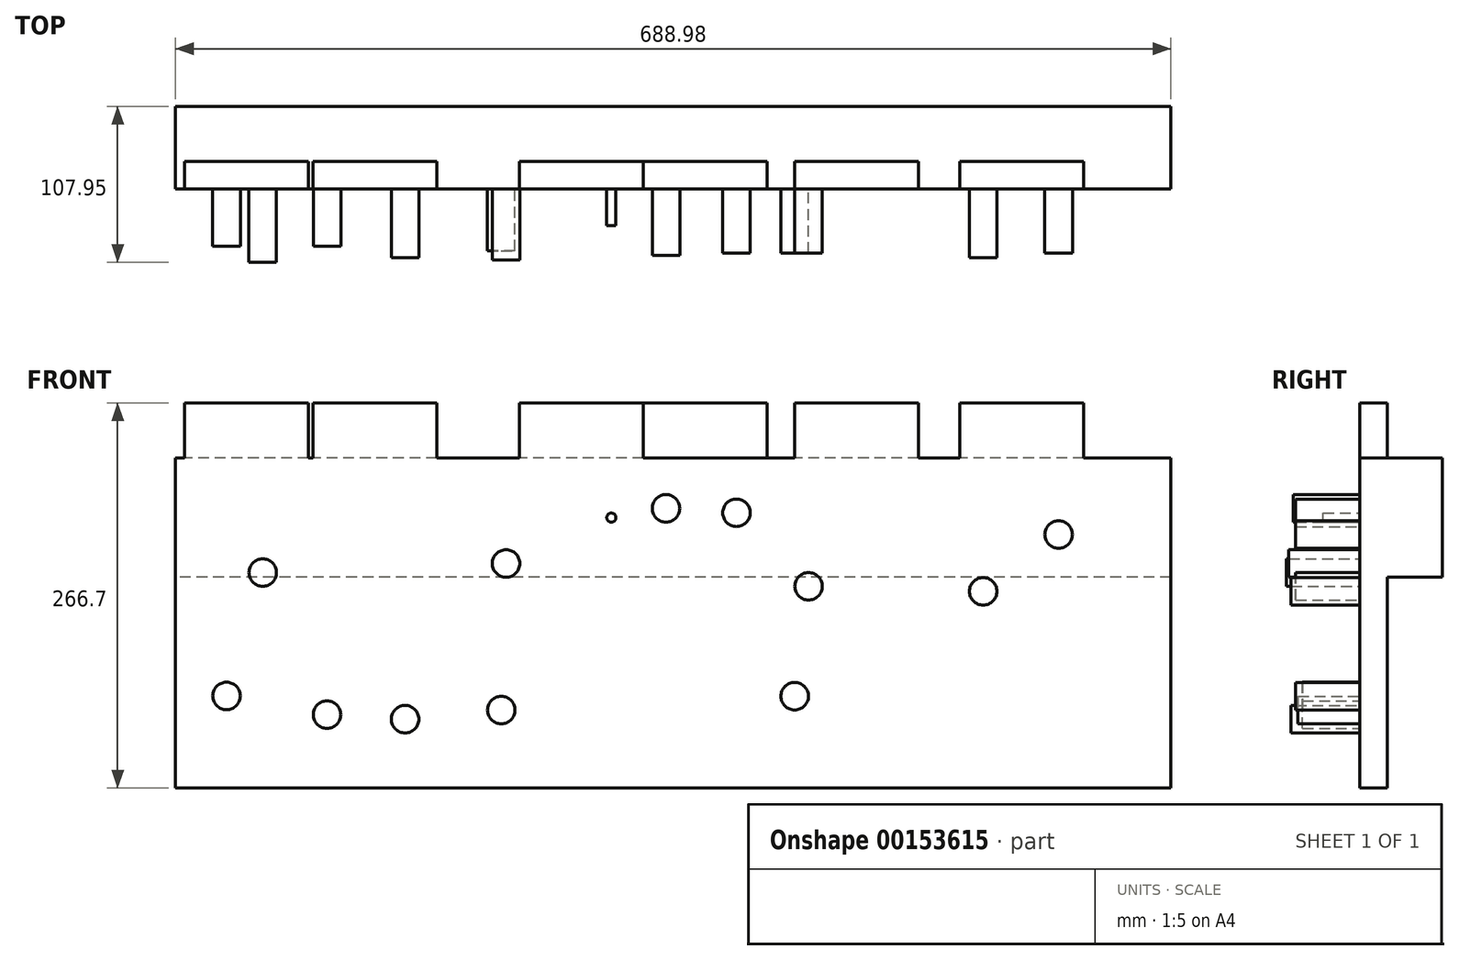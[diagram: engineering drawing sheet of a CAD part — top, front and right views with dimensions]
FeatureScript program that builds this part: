
annotation { "Feature Type Name" : "Feature", "Feature Type Description" : "" }
export const myFeature = defineFeature(function(context is Context, id is Id, definition is map)
    precondition{}
    {
        {
            var Q0;
            Q0=qCreatedBy(makeId("Front.planeOp"),FACE);
            var sketch = newSketch(context, id + "F0", { "sketchPlane" : qUnion([Q0])});
            skLineSegment(sketch, "E0.bottom", {"start": v(344.49, -114.3) * mm, "end": v(-344.49, -114.3) * mm});
            skLineSegment(sketch, "E0.top", {"start": v(344.49, 114.3) * mm, "end": v(-344.49, 114.3) * mm});
            skLineSegment(sketch, "E0.left", {"start": v(344.49, -114.3) * mm, "end": v(344.49, 114.3) * mm});
            skLineSegment(sketch, "E0.right", {"start": v(-344.49, -114.3) * mm, "end": v(-344.49, 114.3) * mm});
            skPoint(sketch, "E0.middle", {"position": v(0, 0) * mm});
            skSolve(sketch);
        }
        {
            var Q0;
            Q0 = qSketchRegion(id + "F0", true);
            extrude(context, id + "F1", {"entities" : qUnion([Q0]), "depth" : 19.05 * mm});
        }
        {
            var Q0;
            Q0=makeQuery(id+"F1.opExtrude","CAP_FACE",FACE,{"disambiguationData":[OSD([sQuery(id+"F0.wireOp",EDGE,"E0.bottom"),sQuery(id+"F0.wireOp",EDGE,"E0.top"),sQuery(id+"F0.wireOp",EDGE,"E0.left"),sQuery(id+"F0.wireOp",EDGE,"E0.right")])],"isStart":true});
            var sketch = newSketch(context, id + "F2", { "sketchPlane" : qUnion([Q0])});
            skLineSegment(sketch, "E1.bottom", {"start": v(-344.49, 114.3) * mm, "end": v(344.49, 114.3) * mm});
            skLineSegment(sketch, "E1.top", {"start": v(-344.49, 31.75) * mm, "end": v(344.49, 31.75) * mm});
            skLineSegment(sketch, "E1.left", {"start": v(-344.49, 114.3) * mm, "end": v(-344.49, 31.75) * mm});
            skLineSegment(sketch, "E1.right", {"start": v(344.49, 114.3) * mm, "end": v(344.49, 31.75) * mm});
            skSolve(sketch);
        }
        {
            var Q0;
            Q0 = qSketchRegion(id + "F2", true);
            extrude(context, id + "F3", {"entities" : qUnion([Q0]), "depth" : 38.1 * mm});
        }
        {
            var Q0;
            Q0=makeQuery(id+"F1.opExtrude","CAP_FACE",FACE,{"disambiguationData":[OSD([sQuery(id+"F0.wireOp",EDGE,"E0.bottom"),sQuery(id+"F0.wireOp",EDGE,"E0.top"),sQuery(id+"F0.wireOp",EDGE,"E0.left"),sQuery(id+"F0.wireOp",EDGE,"E0.right")])],"isStart":false});
            var sketch = newSketch(context, id + "F4", { "sketchPlane" : qUnion([Q0])});
            skCircle(sketch, "E2", {"center": v(-284.18, 34.92) * mm, "radius": 9.53 * mm});
            skCircle(sketch, "E3", {"center": v(-115.78, 41.23) * mm, "radius": 9.53 * mm});
            skCircle(sketch, "E4", {"center": v(-5.07, 79.42) * mm, "radius": 9.52 * mm});
            skCircle(sketch, "E5", {"center": v(43.71, 76.35) * mm, "radius": 9.53 * mm});
            skCircle(sketch, "E6", {"center": v(266.7, 61.27) * mm, "radius": 9.53 * mm});
            skCircle(sketch, "E7", {"center": v(-309.24, -50.51) * mm, "radius": 9.53 * mm});
            skCircle(sketch, "E8", {"center": v(-239.7, -63.5) * mm, "radius": 9.53 * mm});
            skCircle(sketch, "E9", {"center": v(-185.67, -66.62) * mm, "radius": 9.53 * mm});
            skCircle(sketch, "E10", {"center": v(-119.06, -60.3) * mm, "radius": 9.53 * mm});
            skCircle(sketch, "E11", {"center": v(93.64, 25.43) * mm, "radius": 9.53 * mm});
            skCircle(sketch, "E12", {"center": v(214.5, 21.94) * mm, "radius": 9.53 * mm});
            skCircle(sketch, "E13", {"center": v(84.02, -50.69) * mm, "radius": 9.53 * mm});
            skCircle(sketch, "E14", {"center": v(-42.88, 73) * mm, "radius": 3.18 * mm});
            skSolve(sketch);
        }
        {
            var Q0;
            Q0=makeQuery(id+"F4.imprint","IMPRINT",FACE,{"disambiguationData":[TD([[makeQuery(id+"F4.imprint","IMPRINT",EDGE,{"derivedFrom":sQuery(id+"F4.wireOp",EDGE,"E2")}),1.0]])]});
            var Q1;
            Q1=sQuery(id+"F4.wireOp",EDGE,"E2");
            extrude(context, id + "F5", {"entities" : qUnion([Q0]), "operationType" : NewBodyOperationType.ADD, "surfaceEntities" : qUnion([Q1]), "depth" : 50.8 * mm});
        }
        {
            var Q0;
            Q0=makeQuery(id+"F4.imprint","IMPRINT",FACE,{"disambiguationData":[TD([[makeQuery(id+"F4.imprint","IMPRINT",EDGE,{"derivedFrom":sQuery(id+"F4.wireOp",EDGE,"E3")}),1.0]])]});
            var Q1;
            Q1=sQuery(id+"F4.wireOp",EDGE,"E3");
            extrude(context, id + "F6", {"entities" : qUnion([Q0]), "operationType" : NewBodyOperationType.ADD, "surfaceEntities" : qUnion([Q1]), "depth" : 49.2 * mm});
        }
        {
            var Q0;
            Q0=makeQuery(id+"F4.imprint","IMPRINT",FACE,{"disambiguationData":[TD([[makeQuery(id+"F4.imprint","IMPRINT",EDGE,{"derivedFrom":sQuery(id+"F4.wireOp",EDGE,"E4")}),1.0]])]});
            var Q1;
            Q1=sQuery(id+"F4.wireOp",EDGE,"E4");
            extrude(context, id + "F7", {"entities" : qUnion([Q0]), "operationType" : NewBodyOperationType.ADD, "surfaceEntities" : qUnion([Q1]), "depth" : 46.04 * mm});
        }
        {
            var Q0;
            Q0=makeQuery(id+"F4.imprint","IMPRINT",FACE,{"disambiguationData":[TD([[makeQuery(id+"F4.imprint","IMPRINT",EDGE,{"derivedFrom":sQuery(id+"F4.wireOp",EDGE,"E5")}),1.0]])]});
            var Q1;
            Q1=sQuery(id+"F4.wireOp",EDGE,"E5");
            extrude(context, id + "F8", {"entities" : qUnion([Q0]), "operationType" : NewBodyOperationType.ADD, "surfaceEntities" : qUnion([Q1]), "depth" : 44.45 * mm});
        }
        {
            var Q0;
            Q0=makeQuery(id+"F4.imprint","IMPRINT",FACE,{"disambiguationData":[TD([[makeQuery(id+"F4.imprint","IMPRINT",EDGE,{"derivedFrom":sQuery(id+"F4.wireOp",EDGE,"E6")}),1.0]])]});
            var Q1;
            Q1=sQuery(id+"F4.wireOp",EDGE,"E6");
            extrude(context, id + "F9", {"entities" : qUnion([Q0]), "operationType" : NewBodyOperationType.ADD, "surfaceEntities" : qUnion([Q1]), "depth" : 44.45 * mm});
        }
        {
            var Q0;
            Q0=makeQuery(id+"F4.imprint","IMPRINT",FACE,{"disambiguationData":[TD([[makeQuery(id+"F4.imprint","IMPRINT",EDGE,{"derivedFrom":sQuery(id+"F4.wireOp",EDGE,"E7")}),1.0]])]});
            var Q1;
            Q1=sQuery(id+"F4.wireOp",EDGE,"E7");
            extrude(context, id + "F10", {"entities" : qUnion([Q0]), "operationType" : NewBodyOperationType.ADD, "surfaceEntities" : qUnion([Q1]), "depth" : 39.69 * mm});
        }
        {
            var Q0;
            Q0=makeQuery(id+"F4.imprint","IMPRINT",FACE,{"disambiguationData":[TD([[makeQuery(id+"F4.imprint","IMPRINT",EDGE,{"derivedFrom":sQuery(id+"F4.wireOp",EDGE,"E8")}),1.0]])]});
            extrude(context, id + "F11", {"entities" : qUnion([Q0]), "operationType" : NewBodyOperationType.ADD, "depth" : 39.69 * mm});
        }
        {
            var Q0;
            Q0=makeQuery(id+"F4.imprint","IMPRINT",FACE,{"disambiguationData":[TD([[makeQuery(id+"F4.imprint","IMPRINT",EDGE,{"derivedFrom":sQuery(id+"F4.wireOp",EDGE,"E9")}),1.0]])]});
            var Q1;
            Q1=sQuery(id+"F4.wireOp",EDGE,"E9");
            extrude(context, id + "F12", {"entities" : qUnion([Q0]), "operationType" : NewBodyOperationType.ADD, "surfaceEntities" : qUnion([Q1]), "depth" : 47.62 * mm});
        }
        {
            var Q0;
            Q0=makeQuery(id+"F4.imprint","IMPRINT",FACE,{"disambiguationData":[TD([[makeQuery(id+"F4.imprint","IMPRINT",EDGE,{"derivedFrom":sQuery(id+"F4.wireOp",EDGE,"E10")}),1.0]])]});
            extrude(context, id + "F13", {"entities" : qUnion([Q0]), "operationType" : NewBodyOperationType.ADD, "depth" : 42.86 * mm});
        }
        {
            var Q0;
            Q0=makeQuery(id+"F4.imprint","IMPRINT",FACE,{"disambiguationData":[TD([[makeQuery(id+"F4.imprint","IMPRINT",EDGE,{"derivedFrom":sQuery(id+"F4.wireOp",EDGE,"E11")}),1.0]])]});
            extrude(context, id + "F14", {"entities" : qUnion([Q0]), "operationType" : NewBodyOperationType.ADD, "depth" : 44.45 * mm});
        }
        {
            var Q0;
            Q0=makeQuery(id+"F4.imprint","IMPRINT",FACE,{"disambiguationData":[TD([[makeQuery(id+"F4.imprint","IMPRINT",EDGE,{"derivedFrom":sQuery(id+"F4.wireOp",EDGE,"E12")}),1.0]])]});
            extrude(context, id + "F15", {"entities" : qUnion([Q0]), "operationType" : NewBodyOperationType.ADD, "depth" : 47.62 * mm});
        }
        {
            var Q0;
            Q0=makeQuery(id+"F4.imprint","IMPRINT",FACE,{"disambiguationData":[TD([[makeQuery(id+"F4.imprint","IMPRINT",EDGE,{"derivedFrom":sQuery(id+"F4.wireOp",EDGE,"E13")}),1.0]])]});
            extrude(context, id + "F16", {"entities" : qUnion([Q0]), "operationType" : NewBodyOperationType.ADD, "depth" : 44.45 * mm});
        }
        {
            var Q0;
            Q0=makeQuery(id+"F4.imprint","IMPRINT",FACE,{"disambiguationData":[TD([[makeQuery(id+"F4.imprint","IMPRINT",EDGE,{"derivedFrom":sQuery(id+"F4.wireOp",EDGE,"E14")}),1.0]])]});
            extrude(context, id + "F17", {"entities" : qUnion([Q0]), "operationType" : NewBodyOperationType.ADD, "depth" : 25.4 * mm});
        }
        {
            var Q0;
            Q0=makeQuery(id+"F1.opExtrude","SWEPT_FACE",FACE,{"disambiguationData":[OSD([sQuery(id+"F0.wireOp",EDGE,"E0.top")])]});
            var sketch = newSketch(context, id + "F18", { "sketchPlane" : qUnion([Q0])});
            skLineSegment(sketch, "E15.left", {"start": v(-338.14, -19.05) * mm, "end": v(-338.14, -19.05) * mm});
            skLineSegment(sketch, "E15.right", {"start": v(-299.87, -19.05) * mm, "end": v(-299.87, -19.05) * mm});
            skLineSegment(sketch, "E16.bottom", {"start": v(-338.14, -19.05) * mm, "end": v(-252.41, -19.05) * mm});
            skLineSegment(sketch, "E16.top", {"start": v(-338.14, 0) * mm, "end": v(-252.41, 0) * mm});
            skLineSegment(sketch, "E16.left", {"start": v(-338.14, -19.05) * mm, "end": v(-338.14, 0) * mm});
            skLineSegment(sketch, "E16.right", {"start": v(-252.41, -19.05) * mm, "end": v(-252.41, 0) * mm});
            skLineSegment(sketch, "E17", {"start": v(-252.41, -19.05) * mm, "end": v(-249.24, -19.05) * mm, "construction": true});
            skLineSegment(sketch, "E18.bottom", {"start": v(-249.24, -19.05) * mm, "end": v(-163.51, -19.05) * mm});
            skLineSegment(sketch, "E18.top", {"start": v(-249.24, 0) * mm, "end": v(-163.51, 0) * mm});
            skLineSegment(sketch, "E18.left", {"start": v(-249.24, -19.05) * mm, "end": v(-249.24, 0) * mm});
            skLineSegment(sketch, "E18.right", {"start": v(-163.51, -19.05) * mm, "end": v(-163.51, 0) * mm});
            skLineSegment(sketch, "E19", {"start": v(-163.51, -19.05) * mm, "end": v(-106.36, -19.05) * mm, "construction": true});
            skLineSegment(sketch, "E20.bottom", {"start": v(-106.36, -19.05) * mm, "end": v(-20.64, -19.05) * mm});
            skLineSegment(sketch, "E20.top", {"start": v(-106.36, 0) * mm, "end": v(-20.64, 0) * mm});
            skLineSegment(sketch, "E20.left", {"start": v(-106.36, -19.05) * mm, "end": v(-106.36, 0) * mm});
            skLineSegment(sketch, "E20.right", {"start": v(-20.64, -19.05) * mm, "end": v(-20.64, 0) * mm});
            skLineSegment(sketch, "E21.bottom", {"start": v(-20.64, -19.05) * mm, "end": v(65.09, -19.05) * mm});
            skLineSegment(sketch, "E21.top", {"start": v(-20.64, 0) * mm, "end": v(65.09, 0) * mm});
            skLineSegment(sketch, "E21.right", {"start": v(65.09, -19.05) * mm, "end": v(65.09, 0) * mm});
            skLineSegment(sketch, "E22", {"start": v(65.09, -19.05) * mm, "end": v(84.14, -19.05) * mm});
            skLineSegment(sketch, "E23.bottom", {"start": v(84.14, -19.05) * mm, "end": v(169.86, -19.05) * mm});
            skLineSegment(sketch, "E23.top", {"start": v(84.14, 0) * mm, "end": v(169.86, 0) * mm});
            skLineSegment(sketch, "E23.left", {"start": v(84.14, -19.05) * mm, "end": v(84.14, 0) * mm});
            skLineSegment(sketch, "E23.right", {"start": v(169.86, -19.05) * mm, "end": v(169.86, 0) * mm});
            skLineSegment(sketch, "E24", {"start": v(169.86, -19.05) * mm, "end": v(198.44, -19.05) * mm, "construction": true});
            skLineSegment(sketch, "E25.bottom", {"start": v(198.44, -19.05) * mm, "end": v(284.16, -19.05) * mm});
            skLineSegment(sketch, "E25.top", {"start": v(198.44, 0) * mm, "end": v(284.16, 0) * mm});
            skLineSegment(sketch, "E25.left", {"start": v(198.44, -19.05) * mm, "end": v(198.44, 0) * mm});
            skLineSegment(sketch, "E25.right", {"start": v(284.16, -19.05) * mm, "end": v(284.16, 0) * mm});
            skSolve(sketch);
        }
        {
            var Q0;
            Q0=makeQuery(id+"F18.imprint","IMPRINT",FACE,{"disambiguationData":[TD([[makeQuery(id+"F18.imprint","IMPRINT",EDGE,{"derivedFrom":sQuery(id+"F18.wireOp",EDGE,"E16.bottom")}),-1.0]])]});
            extrude(context, id + "F19", {"entities" : qUnion([Q0]), "operationType" : NewBodyOperationType.ADD, "depth" : 38.1 * mm});
        }
        {
            var Q0;
            Q0=makeQuery(id+"F18.imprint","IMPRINT",FACE,{"disambiguationData":[TD([[makeQuery(id+"F18.imprint","IMPRINT",EDGE,{"derivedFrom":sQuery(id+"F18.wireOp",EDGE,"E18.bottom")}),-1.0]])]});
            var Q1;
            Q1=makeQuery(id+"F18.imprint","IMPRINT",FACE,{"disambiguationData":[TD([[makeQuery(id+"F18.imprint","IMPRINT",EDGE,{"derivedFrom":sQuery(id+"F18.wireOp",EDGE,"E20.bottom")}),-1.0]])]});
            extrude(context, id + "F20", {"entities" : qUnion([Q0, Q1]), "operationType" : NewBodyOperationType.ADD, "depth" : 38.1 * mm});
        }
        {
            var Q0;
            Q0=makeQuery(id+"F18.imprint","IMPRINT",FACE,{"disambiguationData":[TD([[makeQuery(id+"F18.imprint","IMPRINT",EDGE,{"derivedFrom":sQuery(id+"F18.wireOp",EDGE,"E21.bottom")}),-1.0]])]});
            extrude(context, id + "F21", {"entities" : qUnion([Q0]), "depth" : 38.1 * mm});
        }
        {
            var Q0;
            Q0=makeQuery(id+"F18.imprint","IMPRINT",FACE,{"disambiguationData":[TD([[makeQuery(id+"F18.imprint","IMPRINT",EDGE,{"derivedFrom":sQuery(id+"F18.wireOp",EDGE,"E23.bottom")}),-1.0]])]});
            var Q1;
            Q1=makeQuery(id+"F18.imprint","IMPRINT",FACE,{"disambiguationData":[TD([[makeQuery(id+"F18.imprint","IMPRINT",EDGE,{"derivedFrom":sQuery(id+"F18.wireOp",EDGE,"E25.bottom")}),-1.0]])]});
            extrude(context, id + "F22", {"entities" : qUnion([Q0, Q1]), "operationType" : NewBodyOperationType.ADD, "depth" : 38.1 * mm});
        }
    });
